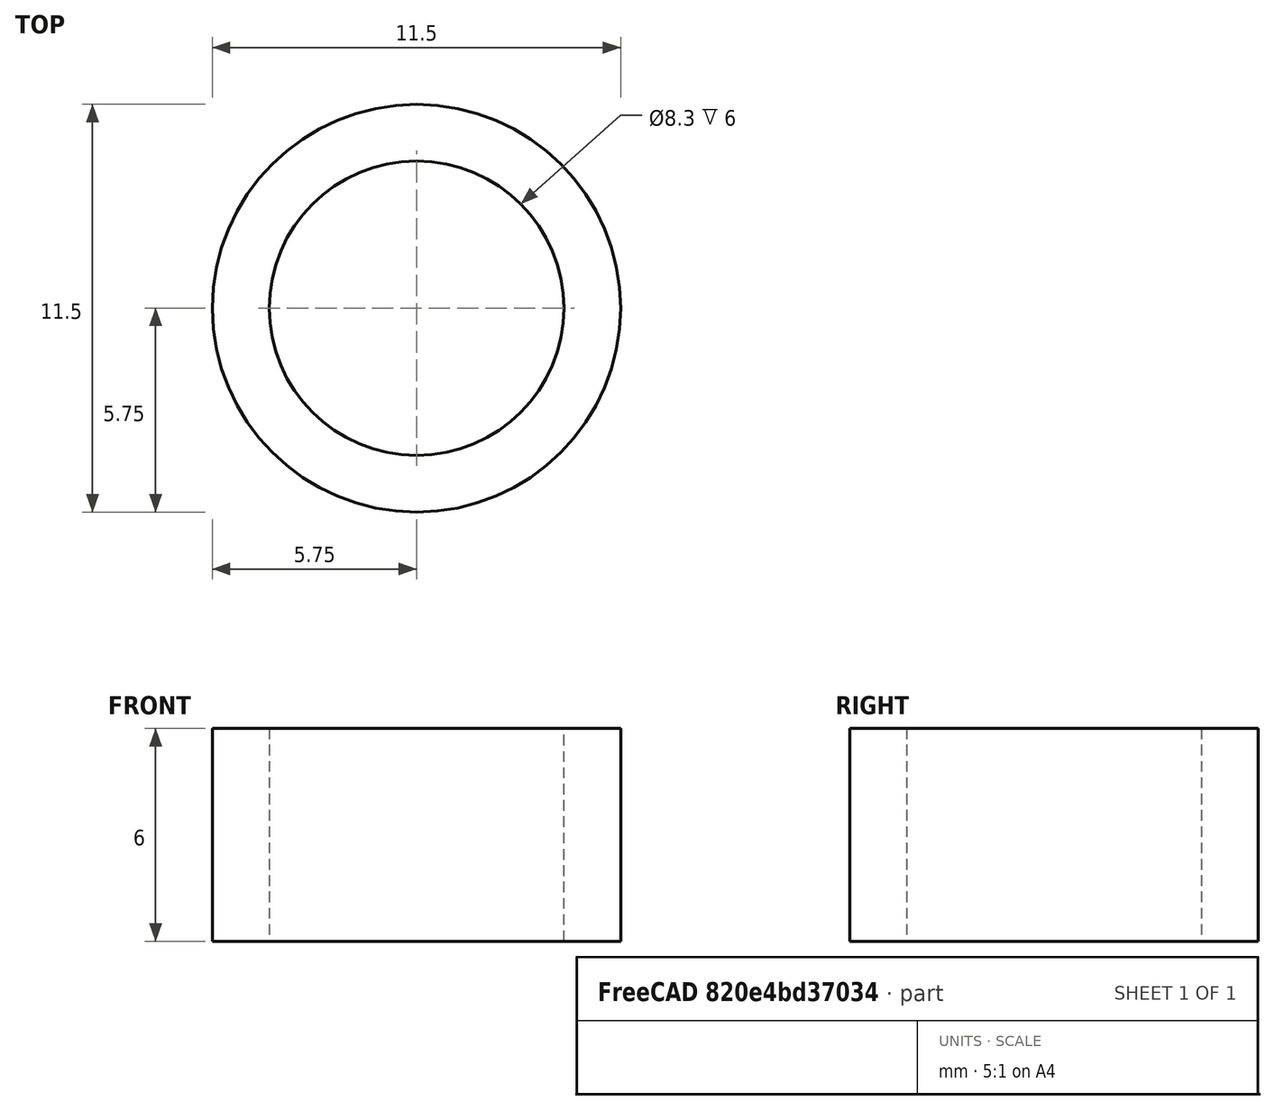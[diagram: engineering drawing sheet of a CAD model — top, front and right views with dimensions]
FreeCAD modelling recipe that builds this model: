
FCSTD DOCUMENT  (FreeCAD 0.21R33668 +26 (Git))
Label: cover_wheel_12-8
License: All rights reserved
LicenseURL: https://en.wikipedia.org/wiki/All_rights_reserved
objects: Sketcher::SketchObject×1, PartDesign::Pad×1, PartDesign::Body×1
note: 4 computed .brp shape members not serialized (recipe doc carries the construction recipe); baked Part::Feature solids carry a one-line shape summary decoded from their .brp

FEATURE [Sketcher::SketchObject] Sketch
  FullyConstrained = true
  MapMode = 5
  Support = -> [XY_Plane]
  sketch-geometry (2):
    g0: Circle CenterX=0 CenterY=0 CenterZ=0 NormalX=0 NormalY=0 NormalZ=1 AngleXU=0 Radius=5.75
    g1: Circle CenterX=0 CenterY=0 CenterZ=0 NormalX=0 NormalY=0 NormalZ=1 AngleXU=0 Radius=4.15
  constraints (4):
    c: Coincident(g0,g-1)
    c: Diameter(g0) = 11.5
    c: Coincident(g1,g0)
    c: Diameter(g1) = 8.3
FEATURE [PartDesign::Pad] Pad
  Direction = (0,0,1)
  Length = 6
  Length2 = 10
  Profile = -> Sketch
  ReferenceAxis = -> Sketch [N_Axis]
  Type = 0
FEATURE [PartDesign::Body] Body
  Group = -> [Sketch,Pad]
  Origin = -> Origin
  Tip = -> Pad
